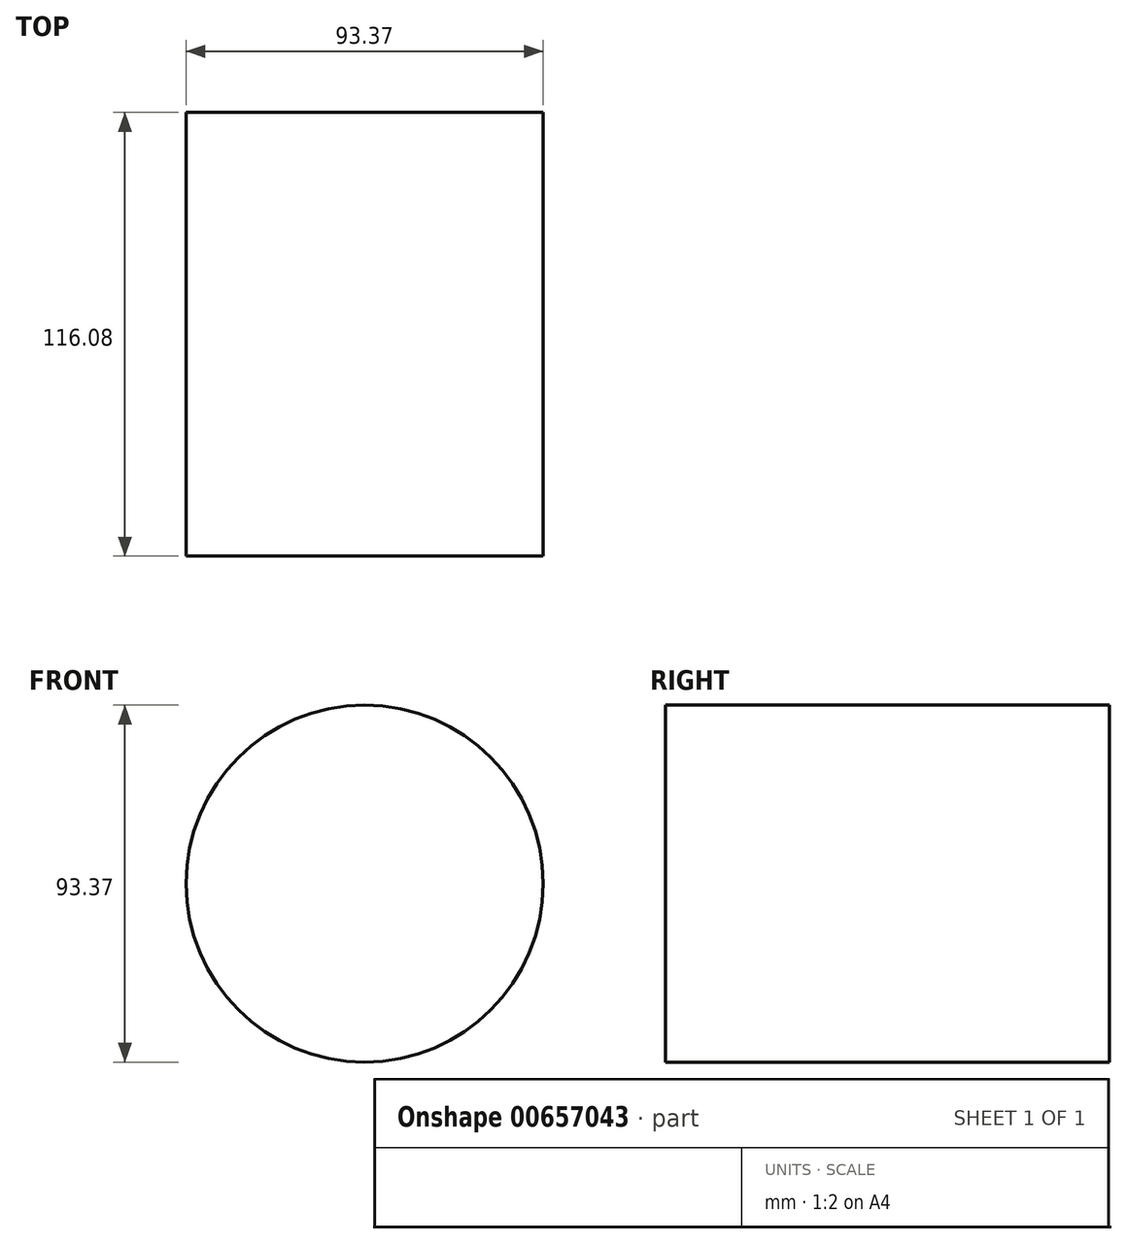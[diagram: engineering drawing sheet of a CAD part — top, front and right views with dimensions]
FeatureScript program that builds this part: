
annotation { "Feature Type Name" : "Feature", "Feature Type Description" : "" }
export const myFeature = defineFeature(function(context is Context, id is Id, definition is map)
    precondition{}
    {
        {
            var Q0;
            Q0=qCreatedBy(makeId("Front.planeOp"),FACE);
            var sketch = newSketch(context, id + "F0", { "sketchPlane" : qUnion([Q0])});
            skCircle(sketch, "E0", {"center": v(-60.6, 38.8) * mm, "radius": 46.68 * mm});
            skSolve(sketch);
        }
        {
            var Q0;
            Q0 = qSketchRegion(id + "F0", true);
            extrude(context, id + "F1", {"entities" : qUnion([Q0]), "depth" : 116.08 * mm, "offsetDistance" : 25.4 * mm});
        }
    });
